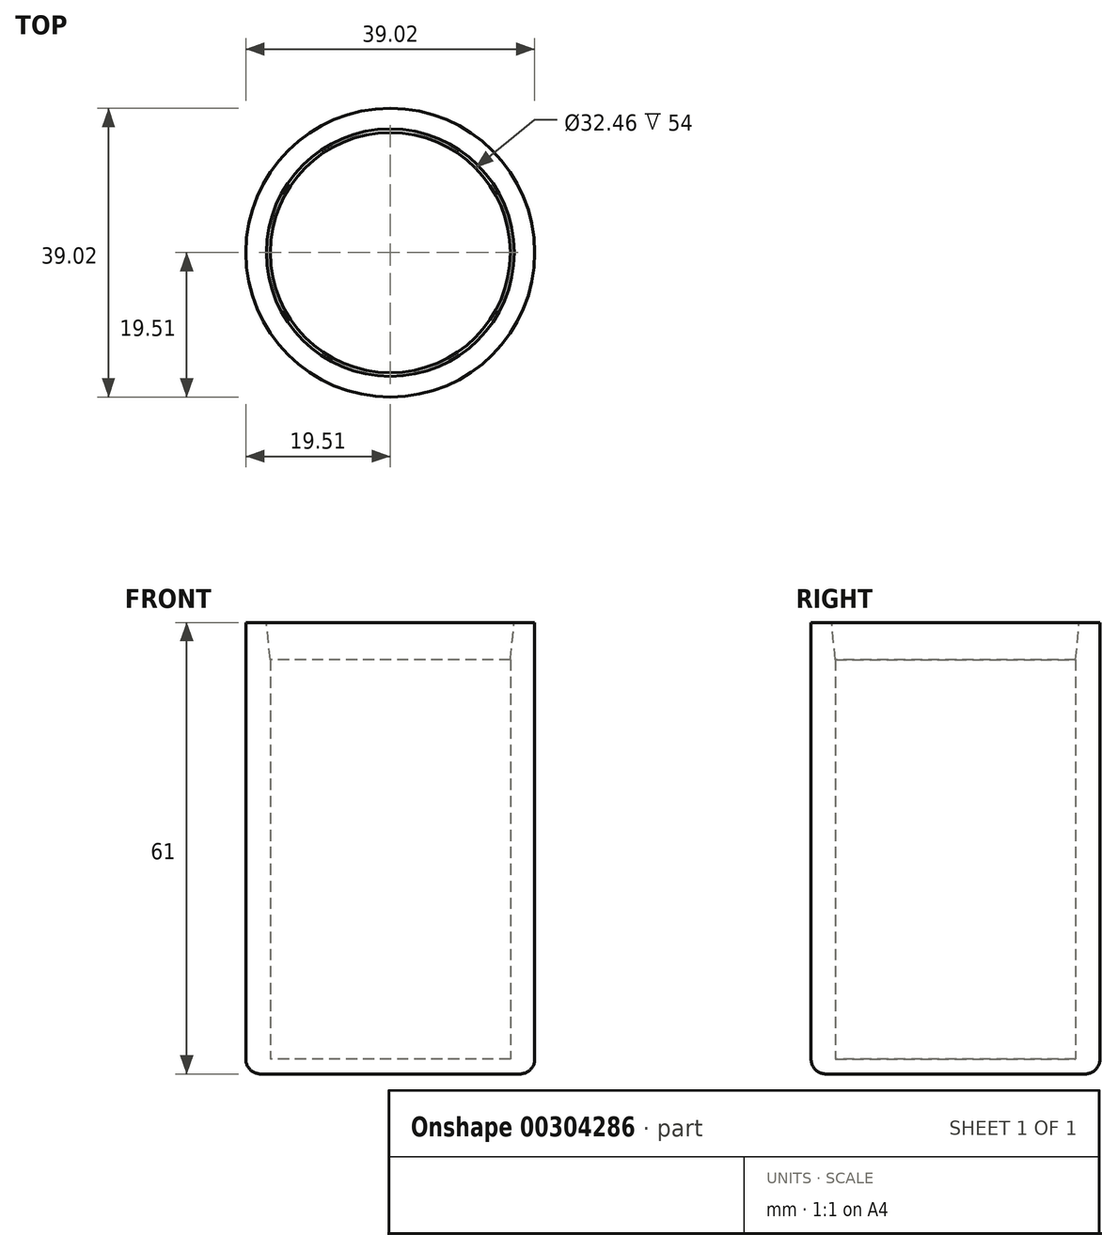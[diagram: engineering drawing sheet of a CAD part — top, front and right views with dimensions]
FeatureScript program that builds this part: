
annotation { "Feature Type Name" : "Feature", "Feature Type Description" : "" }
export const myFeature = defineFeature(function(context is Context, id is Id, definition is map)
    precondition{}
    {
        {
            var Q0;
            Q0=qCreatedBy(makeId("Top.planeOp"),FACE);
            var sketch = newSketch(context, id + "F0", { "sketchPlane" : qUnion([Q0])});
            skCircle(sketch, "E0", {"center": v(0, 0) * mm, "radius": 19.51 * mm});
            skCircle(sketch, "E1", {"center": v(0, 0) * mm, "radius": 16.23 * mm});
            skSolve(sketch);
        }
        {
            var Q0;
            Q0=makeQuery(id+"F0.imprint","IMPRINT",FACE,{"disambiguationData":[TD([[makeQuery(id+"F0.imprint","IMPRINT",EDGE,{"derivedFrom":sQuery(id+"F0.wireOp",EDGE,"E1")}),1.0]])]});
            var Q1;
            Q1=makeQuery(id+"F0.imprint","IMPRINT",FACE,{"disambiguationData":[TD([[makeQuery(id+"F0.imprint","IMPRINT",EDGE,{"derivedFrom":sQuery(id+"F0.wireOp",EDGE,"E0")}),1.0]])]});
            extrude(context, id + "F1", {"entities" : qUnion([Q0, Q1]), "oppositeDirection" : true, "depth" : 2 * mm});
        }
        {
            var Q0;
            Q0=makeQuery(id+"F0.imprint","IMPRINT",FACE,{"disambiguationData":[TD([[makeQuery(id+"F0.imprint","IMPRINT",EDGE,{"derivedFrom":sQuery(id+"F0.wireOp",EDGE,"E0")}),1.0]])]});
            extrude(context, id + "F2", {"entities" : qUnion([Q0]), "operationType" : NewBodyOperationType.ADD, "depth" : 59 * mm});
        }
        {
            var Q0;
            Q0=makeQuery(id+"F1.opExtrude","CAP_EDGE",EDGE,{"disambiguationData":[OSD([sQuery(id+"F0.wireOp",EDGE,"E0")])],"isStart":false});
            var Q1;
            Q1=makeQuery(id+"F2.opExtrude","CAP_EDGE",EDGE,{"disambiguationData":[OSD([sQuery(id+"F0.wireOp",EDGE,"E1")])],"isStart":true});
            fillet(context, id + "F3", {"entities" : qUnion([Q0, Q1]), "radius" : 2 * mm, "tangentPropagation" : true, "allowEdgeOverflow" : false});
        }
        {
            var Q0;
            Q0=makeQuery(id+"F2.opExtrude","CAP_EDGE",EDGE,{"disambiguationData":[OSD([sQuery(id+"F0.wireOp",EDGE,"E1")])],"isStart":false});
            chamfer(context, id + "F4", {"entities" : qUnion([Q0]), "chamferType" : ChamferType.TWO_OFFSETS, "width1" : 5 * mm, "oppositeDirection" : false, "width2" : 0.5 * mm, "tangentPropagation" : true});
        }
    });
